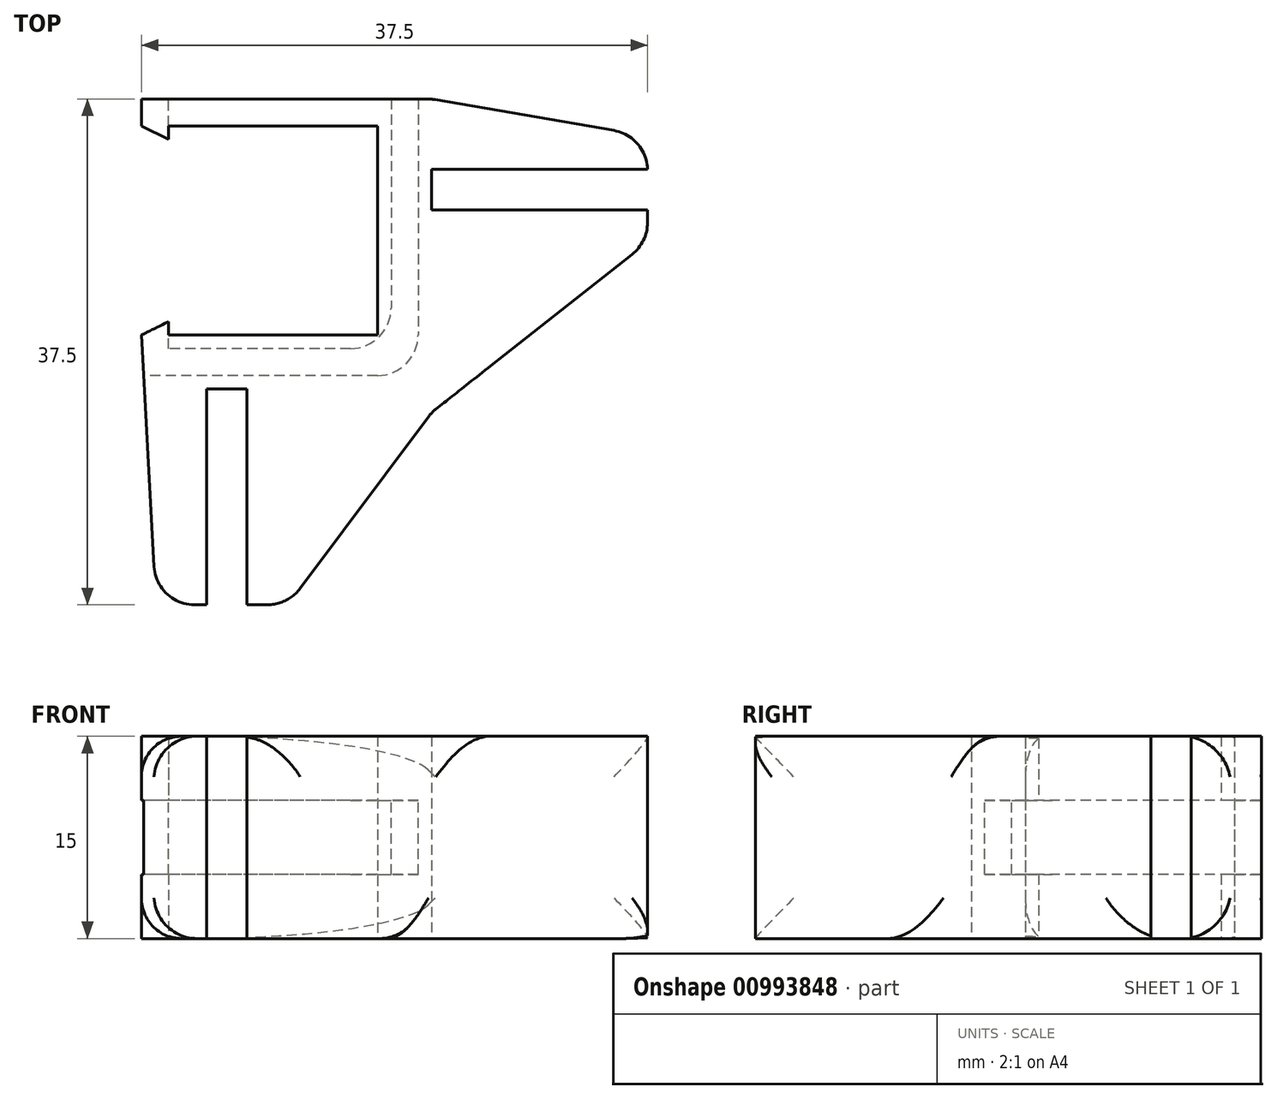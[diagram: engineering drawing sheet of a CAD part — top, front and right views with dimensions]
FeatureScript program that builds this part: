
annotation { "Feature Type Name" : "Feature", "Feature Type Description" : "" }
export const myFeature = defineFeature(function(context is Context, id is Id, definition is map)
    precondition{}
    {
        {
            var Q0;
            Q0=qCreatedBy(makeId("Top.planeOp"),FACE);
            var sketch = newSketch(context, id + "F0", { "sketchPlane" : qUnion([Q0])});
            skLineSegment(sketch, "E0", {"start": v(-5.12, 6.21) * mm, "end": v(10.38, 6.21) * mm});
            skLineSegment(sketch, "E1", {"start": v(10.38, 6.21) * mm, "end": v(10.38, -9.29) * mm});
            skLineSegment(sketch, "E2", {"start": v(10.38, -9.29) * mm, "end": v(-5.12, -9.29) * mm});
            skLineSegment(sketch, "E3", {"start": v(-7.12, -9.29) * mm, "end": v(-6.04, -29.29) * mm});
            skLineSegment(sketch, "E4", {"start": v(-6.04, -29.29) * mm, "end": v(-2.3, -29.29) * mm});
            skLineSegment(sketch, "E5", {"start": v(-2.3, -29.29) * mm, "end": v(-2.3, -13.29) * mm});
            skLineSegment(sketch, "E6", {"start": v(-2.3, -13.29) * mm, "end": v(0.7, -13.29) * mm});
            skLineSegment(sketch, "E7", {"start": v(0.7, -13.29) * mm, "end": v(0.7, -29.29) * mm});
            skLineSegment(sketch, "E8", {"start": v(0.7, -29.29) * mm, "end": v(3.73, -29.29) * mm});
            skLineSegment(sketch, "E9", {"start": v(3.73, -29.29) * mm, "end": v(14.38, -15.03) * mm});
            skLineSegment(sketch, "E10", {"start": v(14.38, 0) * mm, "end": v(14.38, 3) * mm});
            skLineSegment(sketch, "E11", {"start": v(14.38, 8.21) * mm, "end": v(-7.12, 8.21) * mm});
            skLineSegment(sketch, "E12", {"start": v(14.38, 8.21) * mm, "end": v(30.38, 5.45) * mm});
            skLineSegment(sketch, "E13", {"start": v(30.38, 5.45) * mm, "end": v(30.38, 3) * mm});
            skLineSegment(sketch, "E14", {"start": v(30.38, 3) * mm, "end": v(14.38, 3) * mm});
            skLineSegment(sketch, "E15", {"start": v(14.38, 3) * mm, "end": v(14.38, 0) * mm});
            skLineSegment(sketch, "E16", {"start": v(14.38, 0) * mm, "end": v(30.38, 0) * mm});
            skLineSegment(sketch, "E17", {"start": v(30.38, 0) * mm, "end": v(30.38, -2.4) * mm});
            skLineSegment(sketch, "E18", {"start": v(30.38, -2.4) * mm, "end": v(14.38, -15.03) * mm});
            skLineSegment(sketch, "E19", {"start": v(-5.12, 5.21) * mm, "end": v(-5.12, 6.21) * mm});
            skLineSegment(sketch, "E20", {"start": v(-7.12, 6.21) * mm, "end": v(-7.12, 8.21) * mm});
            skLineSegment(sketch, "E21", {"start": v(-5.12, -8.29) * mm, "end": v(-5.12, -9.29) * mm});
            skLineSegment(sketch, "E22", {"start": v(10.38, 6.21) * mm, "end": v(10.38, 8.21) * mm});
            skLineSegment(sketch, "E23", {"start": v(13.38, 8.21) * mm, "end": v(13.38, -12.29) * mm});
            skLineSegment(sketch, "E24", {"start": v(13.38, -12.29) * mm, "end": v(-6.96, -12.29) * mm});
            skLineSegment(sketch, "E25", {"start": v(-5.12, -9.29) * mm, "end": v(-7.12, -9.29) * mm});
            skLineSegment(sketch, "E26", {"start": v(11.38, 8.21) * mm, "end": v(11.38, -10.29) * mm});
            skLineSegment(sketch, "E27", {"start": v(11.38, -10.29) * mm, "end": v(-7.07, -10.29) * mm});
            skLineSegment(sketch, "E28", {"start": v(-5.12, -10.29) * mm, "end": v(-5.12, 8.21) * mm});
            skLineSegment(sketch, "E29", {"start": v(-5.12, -8.29) * mm, "end": v(-7.12, -9.29) * mm});
            skLineSegment(sketch, "E30", {"start": v(-5.12, 6.21) * mm, "end": v(-7.12, 6.21) * mm});
            skLineSegment(sketch, "E31", {"start": v(-7.12, 6.21) * mm, "end": v(-5.12, 5.21) * mm});
            skSolve(sketch);
        }
        {
            var Q0;
            Q0=makeQuery(id+"F0.imprint","IMPRINT",FACE,{"disambiguationData":[TD([[makeQuery(id+"F0.imprint","IMPRINT",EDGE,{"derivedFrom":sQuery(id+"F0.wireOp",EDGE,"E0")}),1.0]])]});
            var Q1;
            {var subQ3=sQuery(id+"F0.wireOp",EDGE,"E4");Q1=makeQuery(id+"F0.imprint","IMPRINT",FACE,{"disambiguationData":[TD([[makeQuery(id+"F0.imprint","IMPRINT",EDGE,{"derivedFrom":subQ3}),1.0]])]});}
            var Q2;
            Q2=makeQuery(id+"F0.imprint","IMPRINT",FACE,{"disambiguationData":[TD([[makeQuery(id+"F0.imprint","IMPRINT",EDGE,{"derivedFrom":sQuery(id+"F0.wireOp",EDGE,"E1")}),1.0]])]});
            var Q3;
            Q3=makeQuery(id+"F0.imprint","IMPRINT",FACE,{"disambiguationData":[TD([[makeQuery(id+"F0.imprint","IMPRINT",EDGE,{"derivedFrom":sQuery(id+"F0.wireOp",EDGE,"a3T7DVUI-DYad-vLGo-VUQ2-JsqKOhsKDFCi")}),-1.0]])]});
            var Q4;
            {var subQ0=sQuery(id+"F0.wireOp",EDGE,"QC6bCrVG-uBQh-5uHJ-CCIM-InmsQJVQocFa");Q4=makeQuery(id+"F0.imprint","IMPRINT",FACE,{"disambiguationData":[TD([[makeQuery(id+"F0.imprint","IMPRINT",EDGE,{"derivedFrom":subQ0}),1.0]])]});}
            var Q5;
            {var subQ1=sQuery(id+"F0.wireOp",EDGE,"E23");Q5=makeQuery(id+"F0.imprint","IMPRINT",FACE,{"disambiguationData":[TD([[makeQuery(id+"F0.imprint","IMPRINT",EDGE,{"derivedFrom":subQ1}),-1.0]])]});}
            var Q6;
            {var subQ0=sQuery(id+"F0.wireOp",EDGE,"E25");Q6=makeQuery(id+"F0.imprint","IMPRINT",FACE,{"disambiguationData":[TD([[makeQuery(id+"F0.imprint","IMPRINT",EDGE,{"derivedFrom":subQ0}),1.0]])]});}
            var Q7;
            {var subQ0=sQuery(id+"F0.wireOp",EDGE,"E25");Q7=makeQuery(id+"F0.imprint","IMPRINT",FACE,{"disambiguationData":[TD([[makeQuery(id+"F0.imprint","IMPRINT",EDGE,{"derivedFrom":subQ0}),-1.0]])]});}
            var Q8;
            {var subQ0=sQuery(id+"F0.wireOp",EDGE,"E30");Q8=makeQuery(id+"F0.imprint","IMPRINT",FACE,{"disambiguationData":[TD([[makeQuery(id+"F0.imprint","IMPRINT",EDGE,{"derivedFrom":subQ0}),1.0]])]});}
            var Q9;
            {var subQ0=sQuery(id+"F0.wireOp",EDGE,"E20");Q9=makeQuery(id+"F0.imprint","IMPRINT",FACE,{"disambiguationData":[TD([[makeQuery(id+"F0.imprint","IMPRINT",EDGE,{"derivedFrom":subQ0}),-1.0]])]});}
            extrude(context, id + "F1", {"entities" : qUnion([Q0, Q1, Q2, Q3, Q4, Q5, Q6, Q7, Q8, Q9]), "depth" : 15 * mm, "offsetDistance" : 25 * mm, "symmetric" : true});
        }
        {
            var Q0;
            {var subQ1=sQuery(id+"F0.wireOp",EDGE,"E23");Q0=makeQuery(id+"F0.imprint","IMPRINT",FACE,{"disambiguationData":[TD([[makeQuery(id+"F0.imprint","IMPRINT",EDGE,{"derivedFrom":subQ1}),-1.0]])]});}
            var Q1;
            Q1=makeQuery(id+"F0.imprint","IMPRINT",FACE,{"disambiguationData":[TD([[makeQuery(id+"F0.imprint","IMPRINT",EDGE,{"derivedFrom":sQuery(id+"F0.wireOp",EDGE,"a3T7DVUI-DYad-vLGo-VUQ2-JsqKOhsKDFCi")}),-1.0]])]});
            var Q2;
            {var subQ0=sQuery(id+"F0.wireOp",EDGE,"E25");Q2=makeQuery(id+"F0.imprint","IMPRINT",FACE,{"disambiguationData":[TD([[makeQuery(id+"F0.imprint","IMPRINT",EDGE,{"derivedFrom":subQ0}),1.0]])]});}
            var Q3;
            {var subQ2=sQuery(id+"F0.wireOp",EDGE,"QC6bCrVG-uBQh-5uHJ-CCIM-InmsQJVQocFa");Q3=makeQuery(id+"F0.imprint","IMPRINT",FACE,{"disambiguationData":[TD([[makeQuery(id+"F0.imprint","IMPRINT",EDGE,{"derivedFrom":subQ2}),1.0]])]});}
            var Q4;
            {var subQ0=sQuery(id+"F0.wireOp",EDGE,"E25");Q4=makeQuery(id+"F0.imprint","IMPRINT",FACE,{"disambiguationData":[TD([[makeQuery(id+"F0.imprint","IMPRINT",EDGE,{"derivedFrom":subQ0}),-1.0]])]});}
            var Q5;
            {var subQ0=sQuery(id+"F0.wireOp",EDGE,"E30");Q5=makeQuery(id+"F0.imprint","IMPRINT",FACE,{"disambiguationData":[TD([[makeQuery(id+"F0.imprint","IMPRINT",EDGE,{"derivedFrom":subQ0}),1.0]])]});}
            var Q6;
            {var subQ0=sQuery(id+"F0.wireOp",EDGE,"E20");Q6=makeQuery(id+"F0.imprint","IMPRINT",FACE,{"disambiguationData":[TD([[makeQuery(id+"F0.imprint","IMPRINT",EDGE,{"derivedFrom":subQ0}),-1.0]])]});}
            extrude(context, id + "F2", {"entities" : qUnion([Q0, Q1, Q2, Q3, Q4, Q5, Q6]), "operationType" : NewBodyOperationType.REMOVE, "oppositeDirection" : true, "depth" : 5.5 * mm, "offsetDistance" : 25 * mm, "symmetric" : true});
        }
        {
            var Q0;
            Q0=makeQuery(id+"F2.boolean.opBoolean","COPY",EDGE,{"derivedFrom":makeQuery(id+"F2.opExtrude","SWEPT_EDGE",EDGE,{"disambiguationData":[OSD([sQuery(id+"F0.wireOp",EDGE,"E23"),sQuery(id+"F0.wireOp",EDGE,"E24")])]})});
            var Q1;
            Q1=makeQuery(id+"F2.boolean.opBoolean","COPY",EDGE,{"derivedFrom":makeQuery(id+"F2.opExtrude","SWEPT_EDGE",EDGE,{"disambiguationData":[OSD([sQuery(id+"F0.wireOp",EDGE,"E26"),sQuery(id+"F0.wireOp",EDGE,"E27")])]})});
            fillet(context, id + "F3", {"entities" : qUnion([Q0, Q1]), "tangentPropagation" : true, "radius" : 3 * mm, "defaultsChanged" : true, "vertexSettings" : [], "allowEdgeOverflow" : false});
        }
        {
            var Q0;
            Q0=makeQuery(id+"F1.opExtrude","SWEPT_EDGE",EDGE,{"disambiguationData":[OSD([sQuery(id+"F0.wireOp",EDGE,"E9"),sQuery(id+"F0.wireOp",EDGE,"E18")])]});
            var Q1;
            Q1=makeQuery(id+"F1.opExtrude","CAP_EDGE",EDGE,{"disambiguationData":[OSD([sQuery(id+"F0.wireOp",EDGE,"E9")])],"isStart":false});
            var Q2;
            Q2=makeQuery(id+"F1.opExtrude","CAP_EDGE",EDGE,{"disambiguationData":[OSD([sQuery(id+"F0.wireOp",EDGE,"E18")])],"isStart":true});
            var Q3;
            Q3=makeQuery(id+"F1.opExtrude","SWEPT_EDGE",EDGE,{"disambiguationData":[OSD([sQuery(id+"F0.wireOp",EDGE,"E11"),sQuery(id+"F0.wireOp",EDGE,"E12")])]});
            var Q4;
            Q4=makeQuery(id+"F1.opExtrude","CAP_EDGE",EDGE,{"disambiguationData":[OSD([sQuery(id+"F0.wireOp",EDGE,"E12")])],"isStart":false});
            var Q5;
            Q5=makeQuery(id+"F1.opExtrude","CAP_EDGE",EDGE,{"disambiguationData":[OSD([sQuery(id+"F0.wireOp",EDGE,"E12")])],"isStart":true});
            var Q6;
            Q6=makeQuery(id+"F1.opExtrude","CAP_EDGE",EDGE,{"disambiguationData":[OSD([sQuery(id+"F0.wireOp",EDGE,"E3")])],"isStart":false});
            var Q7;
            Q7=makeQuery(id+"F1.opExtrude","CAP_EDGE",EDGE,{"disambiguationData":[OSD([sQuery(id+"F0.wireOp",EDGE,"E3")])],"isStart":true});
            var Q8;
            Q8=makeQuery(id+"F1.opExtrude","SWEPT_EDGE",EDGE,{"disambiguationData":[OSD([sQuery(id+"F0.wireOp",EDGE,"E8"),sQuery(id+"F0.wireOp",EDGE,"E9")])]});
            var Q9;
            Q9=makeQuery(id+"F1.opExtrude","SWEPT_EDGE",EDGE,{"disambiguationData":[OSD([sQuery(id+"F0.wireOp",EDGE,"E3"),sQuery(id+"F0.wireOp",EDGE,"E4")])]});
            var Q10;
            Q10=makeQuery(id+"F1.opExtrude","SWEPT_EDGE",EDGE,{"disambiguationData":[OSD([sQuery(id+"F0.wireOp",EDGE,"E17"),sQuery(id+"F0.wireOp",EDGE,"E18")])]});
            var Q11;
            Q11=makeQuery(id+"F1.opExtrude","SWEPT_EDGE",EDGE,{"disambiguationData":[OSD([sQuery(id+"F0.wireOp",EDGE,"E12"),sQuery(id+"F0.wireOp",EDGE,"E13")])]});
            fillet(context, id + "F4", {"entities" : qUnion([Q0, Q1, Q2, Q3, Q4, Q5, Q6, Q7, Q8, Q9, Q10, Q11]), "tangentPropagation" : true, "radius" : 3 * mm, "defaultsChanged" : false, "vertexSettings" : [], "allowEdgeOverflow" : false});
        }
    });
